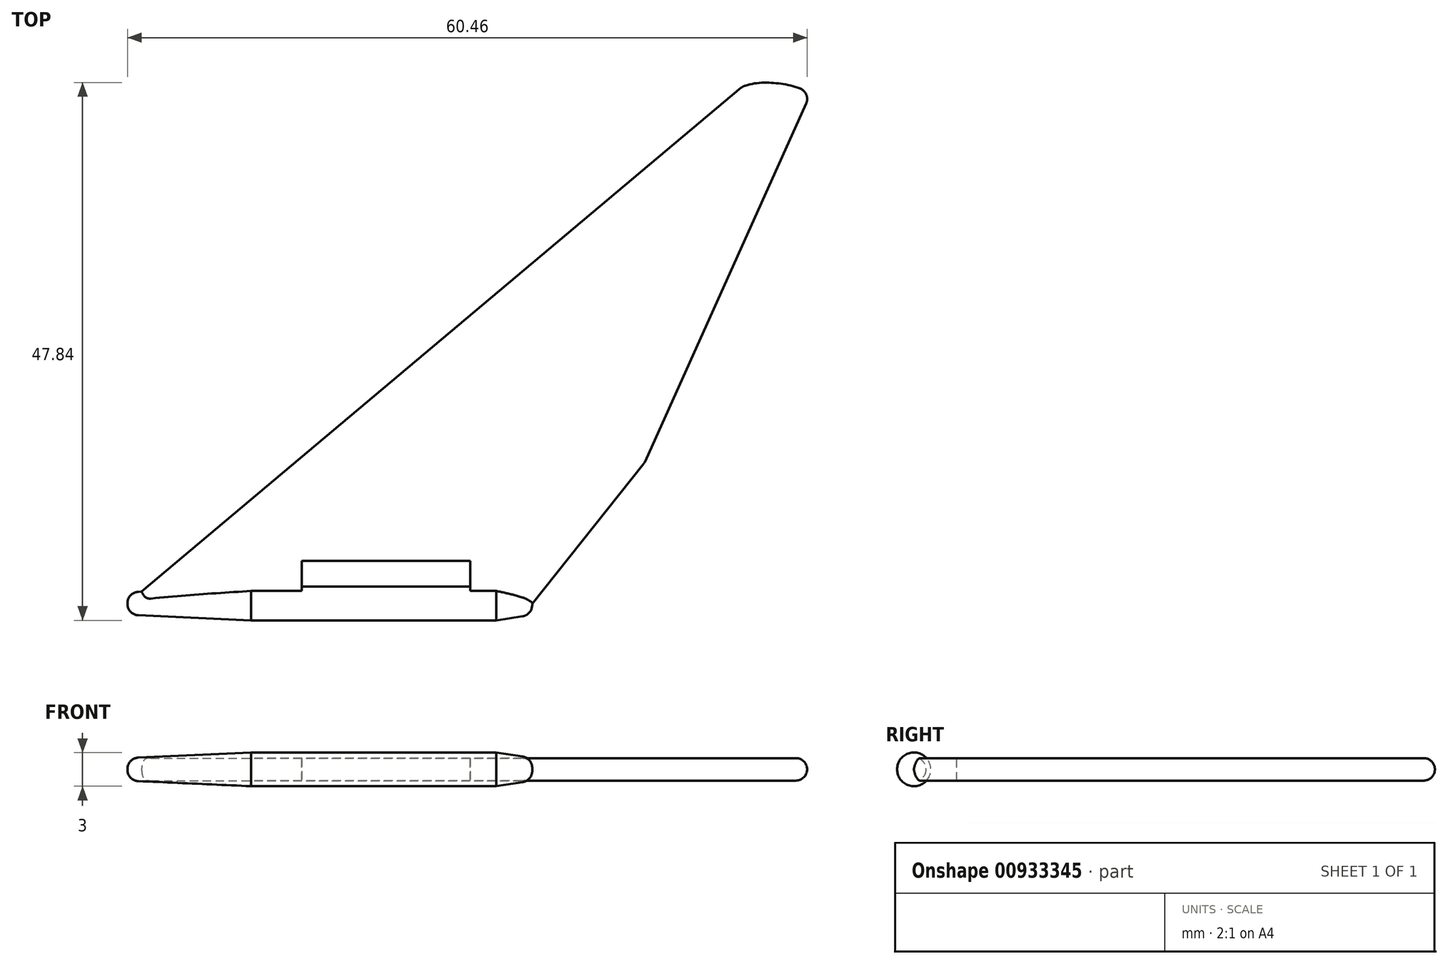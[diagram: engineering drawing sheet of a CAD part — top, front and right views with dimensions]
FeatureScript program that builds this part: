
annotation { "Feature Type Name" : "Feature", "Feature Type Description" : "" }
export const myFeature = defineFeature(function(context is Context, id is Id, definition is map)
    precondition{}
    {
        {
            var Q0;
            Q0=qCreatedBy(makeId("Top.planeOp"),FACE);
            var sketch = newSketch(context, id + "F0", { "sketchPlane" : qUnion([Q0])});
            skLineSegment(sketch, "E0", {"start": v(-18, 0) * mm, "end": v(18, 0) * mm});
            skLineSegment(sketch, "E1", {"start": v(-18, 0) * mm, "end": v(36.74, 46) * mm});
            skLineSegment(sketch, "E2", {"start": v(42.76, 45.33) * mm, "end": v(27.98, 12.5) * mm});
            skLineSegment(sketch, "E3", {"start": v(27.98, 12.5) * mm, "end": v(18, 0) * mm});
            skFitSpline(sketch, "E4", {"points": [v(36.74, 46) * mm, v(42.76, 45.33) * mm], "startDerivative": vector(6.5, 2.42) * mm, "endDerivative": vector(2.29, -1.98) * mm});
            skSolve(sketch);
        }
        {
            var Q0;
            Q0 = qSketchRegion(id + "F0", true);
            extrude(context, id + "F1", {"entities" : qUnion([Q0]), "depth" : 2 * mm, "offsetDistance" : 25 * mm, "symmetric" : true});
        }
        {
            var Q0;
            Q0=qCreatedBy(makeId("Right.planeOp"),FACE);
            var sketch = newSketch(context, id + "F2", { "sketchPlane" : qUnion([Q0])});
            skCircle(sketch, "E5", {"center": v(0, 0) * mm, "radius": 1.5 * mm});
            skSolve(sketch);
        }
        {
            var Q0;
            Q0 = qSketchRegion(id + "F2", true);
            extrude(context, id + "F3", {"entities" : qUnion([Q0]), "depth" : 14.8 * mm, "offsetDistance" : 25 * mm});
        }
        {
            var Q0;
            Q0 = qSketchRegion(id + "F2", true);
            extrude(context, id + "F4", {"entities" : qUnion([Q0]), "operationType" : NewBodyOperationType.ADD, "oppositeDirection" : true, "depth" : 7 * mm, "offsetDistance" : 25 * mm});
        }
        {
            var Q0;
            {var subQ1=sQuery(id+"F0.wireOp",EDGE,"E3");var subQ4=sQuery(id+"F0.wireOp",EDGE,"E0");Q0=makeQuery(id+"F3.boolean.opBoolean","SPLIT",FACE,{"disambiguationData":[TD([makeQuery(id+"F1.opExtrude","SWEPT_FACE",FACE,{"disambiguationData":[OSD([subQ1])]})])],"derivedFrom":makeQuery(id+"F1.opExtrude","SWEPT_FACE",FACE,{"disambiguationData":[OSD([subQ4])]})});}
            var sketch = newSketch(context, id + "F5", { "sketchPlane" : qUnion([Q0])});
            skLineSegment(sketch, "E6.0", {"start": v(14.8, 1.5) * mm, "end": v(14.8, -1.5) * mm});
            skLineSegment(sketch, "E7", {"start": v(14.8, 1.5) * mm, "end": v(18, 1) * mm});
            skLineSegment(sketch, "E8", {"start": v(14.8, 0) * mm, "end": v(18, 0) * mm});
            skLineSegment(sketch, "E9", {"start": v(18, 0) * mm, "end": v(18, 1) * mm});
            skSolve(sketch);
        }
        {
            var Q0;
            Q0 = qSketchRegion(id + "F5", true);
            var Q1;
            Q1=sQuery(id+"F5.wireOp",EDGE,"E8");
            revolve(context, id + "F6", {"operationType" : NewBodyOperationType.ADD, "surfaceOperationType" : NewSurfaceOperationType.NEW, "entities" : qUnion([Q0]), "axis" : qUnion([Q1]), "revolveType" : RevolveType.FULL});
        }
        {
            var Q0;
            {var subQ3=sQuery(id+"F0.wireOp",EDGE,"E1");var subQ4=sQuery(id+"F0.wireOp",EDGE,"E0");Q0=makeQuery(id+"F3.boolean.opBoolean","SPLIT",FACE,{"disambiguationData":[TD([makeQuery(id+"F1.opExtrude","SWEPT_FACE",FACE,{"disambiguationData":[OSD([subQ3])]})])],"derivedFrom":makeQuery(id+"F1.opExtrude","SWEPT_FACE",FACE,{"disambiguationData":[OSD([subQ4])]})});}
            var sketch = newSketch(context, id + "F7", { "sketchPlane" : qUnion([Q0])});
            skLineSegment(sketch, "E10.0", {"start": v(-7, 1.5) * mm, "end": v(-7, -1.5) * mm});
            skLineSegment(sketch, "E11", {"start": v(-7, 0) * mm, "end": v(-18, 0) * mm});
            skLineSegment(sketch, "E12", {"start": v(-18, 0) * mm, "end": v(-18, 1) * mm});
            skLineSegment(sketch, "E13", {"start": v(-18, 1) * mm, "end": v(-7, 1.5) * mm});
            skSolve(sketch);
        }
        {
            var Q0;
            Q0 = qSketchRegion(id + "F7", true);
            var Q1;
            Q1=sQuery(id+"F7.wireOp",EDGE,"E11");
            revolve(context, id + "F8", {"operationType" : NewBodyOperationType.ADD, "surfaceOperationType" : NewSurfaceOperationType.NEW, "entities" : qUnion([Q0]), "axis" : qUnion([Q1]), "revolveType" : RevolveType.FULL});
        }
        {
            var Q0;
            Q0=makeQuery(id+"F1.opExtrude","CAP_FACE",FACE,{"disambiguationData":[OSD([sQuery(id+"F0.wireOp",EDGE,"E0"),sQuery(id+"F0.wireOp",EDGE,"E1"),sQuery(id+"F0.wireOp",EDGE,"E2"),sQuery(id+"F0.wireOp",EDGE,"E3"),sQuery(id+"F0.wireOp",EDGE,"E4")])],"isStart":false});
            var sketch = newSketch(context, id + "F9", { "sketchPlane" : qUnion([Q0])});
            skPoint(sketch, "E14.0", {"position": v(18, 0) * mm});
            skLineSegment(sketch, "E15.bottom", {"start": v(12.5, 2.56) * mm, "end": v(-2.5, 2.56) * mm});
            skLineSegment(sketch, "E15.top", {"start": v(12.5, 3.8) * mm, "end": v(-2.5, 3.8) * mm});
            skLineSegment(sketch, "E15.left", {"start": v(12.5, 2.56) * mm, "end": v(12.5, 3.8) * mm});
            skLineSegment(sketch, "E15.right", {"start": v(-2.5, 2.56) * mm, "end": v(-2.5, 3.8) * mm});
            skLineSegment(sketch, "E16", {"start": v(14.8, -1.5) * mm, "end": v(-7, -1.5) * mm, "construction": true});
            skSolve(sketch);
        }
        {
            var Q0;
            Q0 = qSketchRegion(id + "F9", true);
            extrude(context, id + "F10", {"entities" : qUnion([Q0]), "operationType" : NewBodyOperationType.REMOVE, "endBound" : BoundingType.THROUGH_ALL, "oppositeDirection" : true, "depth" : 25 * mm, "offsetDistance" : 25 * mm});
        }
        {
            var Q0;
            Q0=makeQuery(id+"F10.boolean.opBoolean","COPY",FACE,{"derivedFrom":makeQuery(id+"F10.opExtrude","SWEPT_FACE",FACE,{"disambiguationData":[OSD([sQuery(id+"F9.wireOp",EDGE,"E15.bottom")])]})});
            var Q1;
            {var subQ0=sQuery(id+"F2.wireOp",EDGE,"E5");Q1=makeQuery(id+"F4.boolean.opBoolean","MERGE",FACE,{"derivedFrom":[makeQuery(id+"F3.opExtrude","SWEPT_FACE",FACE,{"disambiguationData":[OSD([subQ0])]}),makeQuery(id+"F4.opExtrude","SWEPT_FACE",FACE,{"disambiguationData":[OSD([subQ0])]})]});}
            var Q2;
            Q2=makeQuery(id+"F3.opExtrude","SWEPT_BODY",BODY,{"disambiguationData":[OSD([sQuery(id+"F2.wireOp",EDGE,"E5")])]});
            extrude(context, id + "F11", {"entities" : qUnion([Q0]), "operationType" : NewBodyOperationType.REMOVE, "endBound" : BoundingType.UP_TO_SURFACE, "oppositeDirection" : true, "depth" : 25 * mm, "endBoundEntityFace" : qUnion([Q1]), "endBoundEntityBody" : qUnion([Q2]), "offsetDistance" : 25 * mm});
        }
        {
            var Q0;
            Q0=makeQuery(id+"F1.opExtrude","SWEPT_FACE",FACE,{"disambiguationData":[OSD([sQuery(id+"F0.wireOp",EDGE,"E4")])]});
            var Q1;
            Q1=makeQuery(id+"F1.opExtrude","SWEPT_FACE",FACE,{"disambiguationData":[OSD([sQuery(id+"F0.wireOp",EDGE,"E2")])]});
            var Q2;
            Q2=makeQuery(id+"F1.opExtrude","CAP_EDGE",EDGE,{"disambiguationData":[OSD([sQuery(id+"F0.wireOp",EDGE,"E3")])],"isStart":false});
            var Q3;
            Q3=makeQuery(id+"F1.opExtrude","CAP_EDGE",EDGE,{"disambiguationData":[OSD([sQuery(id+"F0.wireOp",EDGE,"E3")])],"isStart":true});
            var Q4;
            Q4=makeQuery(id+"F1.opExtrude","CAP_EDGE",EDGE,{"disambiguationData":[OSD([sQuery(id+"F0.wireOp",EDGE,"E1")])],"isStart":true});
            var Q5;
            Q5=makeQuery(id+"F1.opExtrude","CAP_EDGE",EDGE,{"disambiguationData":[OSD([sQuery(id+"F0.wireOp",EDGE,"E1")])],"isStart":false});
            fillet(context, id + "F12", {"entities" : qUnion([Q0, Q1, Q2, Q3, Q4, Q5]), "radius" : 1 * mm, "allowEdgeOverflow" : false});
        }
        {
            var Q0;
            Q0=makeQuery(id+"F8.opRevolve","SWEPT_FACE",FACE,{"disambiguationData":[OSD([sQuery(id+"F7.wireOp",EDGE,"E12")])]});
            fillet(context, id + "F13", {"entities" : qUnion([Q0]), "radius" : 1 * mm, "tangentPropagation" : true, "allowEdgeOverflow" : false});
        }
        {
            var Q0;
            Q0=makeQuery(id+"F6.opRevolve","SWEPT_EDGE",EDGE,{"disambiguationData":[OSD([sQuery(id+"F0.wireOp",EDGE,"E0"),sQuery(id+"F5.wireOp",EDGE,"E7"),sQuery(id+"F5.wireOp",EDGE,"E9")])]});
            fillet(context, id + "F14", {"entities" : qUnion([Q0]), "radius" : 1 * mm, "tangentPropagation" : true, "allowEdgeOverflow" : false});
        }
    });
